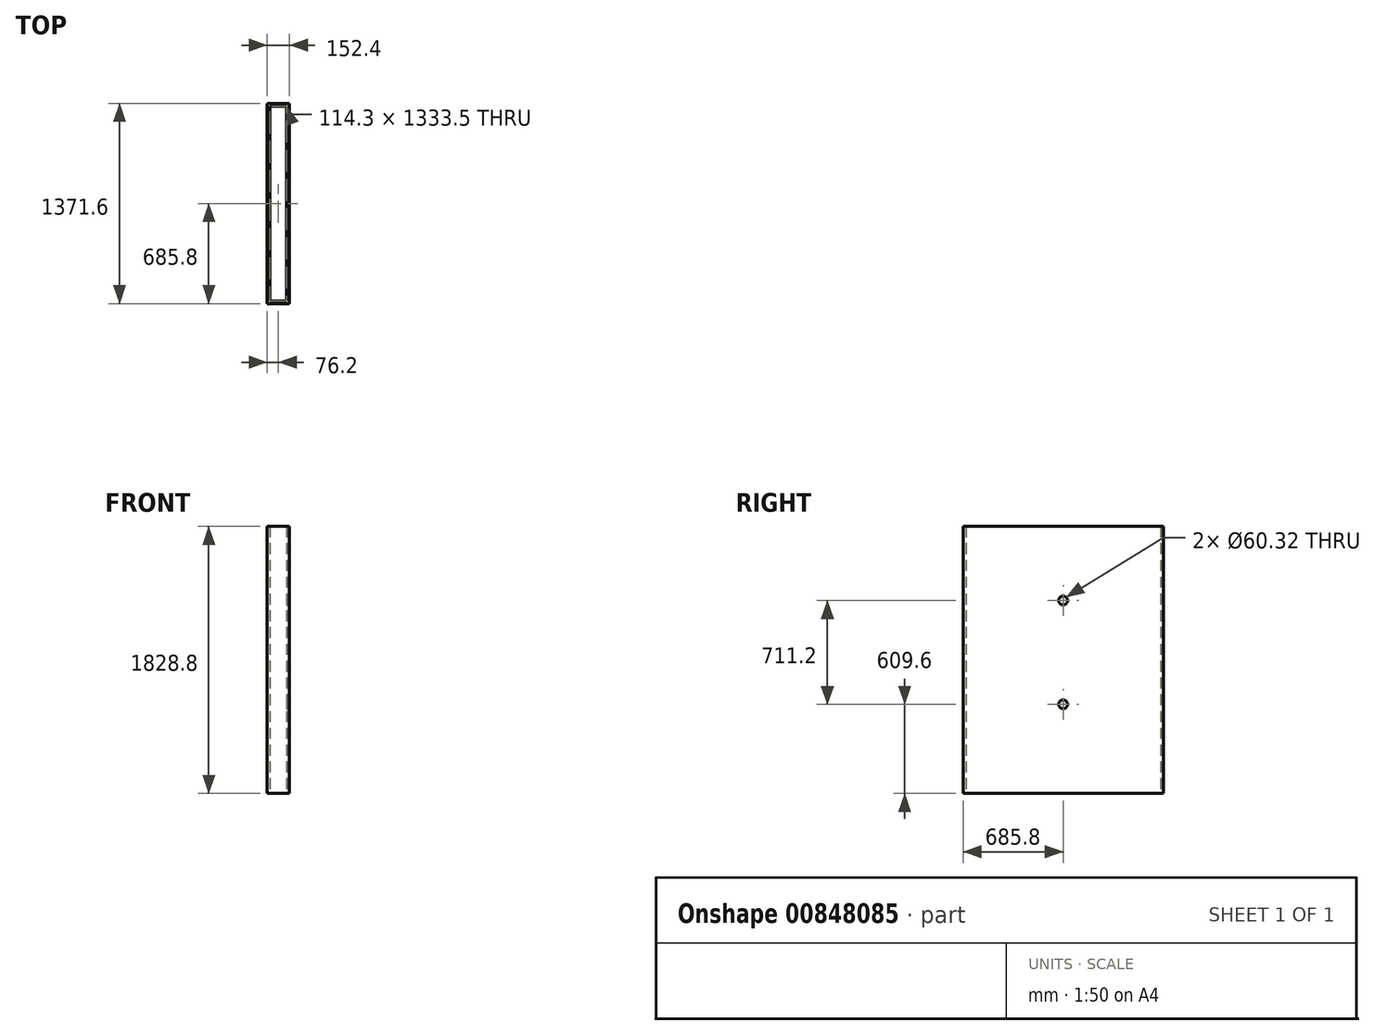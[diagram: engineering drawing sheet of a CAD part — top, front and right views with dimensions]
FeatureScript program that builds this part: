
annotation { "Feature Type Name" : "Feature", "Feature Type Description" : "" }
export const myFeature = defineFeature(function(context is Context, id is Id, definition is map)
    precondition{}
    {
        {
            var Q0;
            Q0=qCreatedBy(makeId("Top.planeOp"),FACE);
            var sketch = newSketch(context, id + "F0", { "sketchPlane" : qUnion([Q0])});
            skLineSegment(sketch, "E0.bottom", {"start": v(76.2, 685.8) * mm, "end": v(-76.2, 685.8) * mm});
            skLineSegment(sketch, "E0.top", {"start": v(76.2, -685.8) * mm, "end": v(-76.2, -685.8) * mm});
            skLineSegment(sketch, "E0.left", {"start": v(76.2, 685.8) * mm, "end": v(76.2, -685.8) * mm});
            skLineSegment(sketch, "E0.right", {"start": v(-76.2, 685.8) * mm, "end": v(-76.2, -685.8) * mm});
            skPoint(sketch, "E0.middle", {"position": v(0, 0) * mm});
            skLineSegment(sketch, "E1.bottom", {"start": v(57.15, -666.75) * mm, "end": v(-57.15, -666.75) * mm});
            skLineSegment(sketch, "E1.top", {"start": v(57.15, 666.75) * mm, "end": v(-57.15, 666.75) * mm});
            skLineSegment(sketch, "E1.left", {"start": v(57.15, -666.75) * mm, "end": v(57.15, 666.75) * mm});
            skLineSegment(sketch, "E1.right", {"start": v(-57.15, -666.75) * mm, "end": v(-57.15, 666.75) * mm});
            skSolve(sketch);
        }
        {
            var Q0;
            Q0=makeQuery(id+"F0.imprint","IMPRINT",FACE,{"disambiguationData":[TD([[makeQuery(id+"F0.imprint","IMPRINT",EDGE,{"derivedFrom":sQuery(id+"F0.wireOp",EDGE,"E0.bottom")}),1.0]])]});
            extrude(context, id + "F1", {"entities" : qUnion([Q0]), "depth" : 1828.8 * mm, "offsetDistance" : 25.4 * mm});
        }
        {
            var Q0;
            Q0=makeQuery(id+"F1.opExtrude","SWEPT_FACE",FACE,{"disambiguationData":[OSD([sQuery(id+"F0.wireOp",EDGE,"E0.left")])]});
            var sketch = newSketch(context, id + "F2", { "sketchPlane" : qUnion([Q0])});
            skLineSegment(sketch, "E2", {"start": v(0, 1828.8) * mm, "end": v(0, 1320.8) * mm});
            skLineSegment(sketch, "E3", {"start": v(0, 0) * mm, "end": v(0, 609.6) * mm});
            skCircle(sketch, "E4", {"center": v(0, 1320.8) * mm, "radius": 30.16 * mm});
            skCircle(sketch, "E5", {"center": v(0, 609.6) * mm, "radius": 30.16 * mm});
            skLineSegment(sketch, "E6", {"start": v(0, 0) * mm, "end": v(0, 101.6) * mm});
            skLineSegment(sketch, "E7", {"start": v(0, 101.6) * mm, "end": v(0, 419.1) * mm});
            skLineSegment(sketch, "E8.bottom", {"start": v(133.35, 419.1) * mm, "end": v(-133.35, 419.1) * mm});
            skLineSegment(sketch, "E8.top", {"start": v(133.35, 101.6) * mm, "end": v(-133.35, 101.6) * mm});
            skLineSegment(sketch, "E8.left", {"start": v(133.35, 419.1) * mm, "end": v(133.35, 101.6) * mm});
            skLineSegment(sketch, "E8.right", {"start": v(-133.35, 419.1) * mm, "end": v(-133.35, 101.6) * mm});
            skPoint(sketch, "E8.middle", {"position": v(0, 260.35) * mm});
            skSolve(sketch);
        }
        {
            var Q0;
            Q0=makeQuery(id+"F2.imprint","IMPRINT",FACE,{"disambiguationData":[TD([[makeQuery(id+"F2.imprint","IMPRINT",EDGE,{"derivedFrom":sQuery(id+"F2.wireOp",EDGE,"E4")}),1.0]])]});
            var Q1;
            Q1=makeQuery(id+"F2.imprint","IMPRINT",FACE,{"disambiguationData":[TD([[makeQuery(id+"F2.imprint","IMPRINT",EDGE,{"derivedFrom":sQuery(id+"F2.wireOp",EDGE,"E5")}),1.0]])]});
            var Q2;
            {var subQ0=sQuery(id+"F2.wireOp",EDGE,"E7");Q2=makeQuery(id+"F2.imprint","IMPRINT",FACE,{"disambiguationData":[TD([[makeQuery(id+"F2.imprint","IMPRINT",EDGE,{"derivedFrom":subQ0}),1.0]])]});}
            var Q3;
            {var subQ0=sQuery(id+"F2.wireOp",EDGE,"E7");Q3=makeQuery(id+"F2.imprint","IMPRINT",FACE,{"disambiguationData":[TD([[makeQuery(id+"F2.imprint","IMPRINT",EDGE,{"derivedFrom":subQ0}),-1.0]])]});}
            extrude(context, id + "F3", {"entities" : qUnion([Q0, Q1, Q2, Q3]), "operationType" : NewBodyOperationType.REMOVE, "oppositeDirection" : true, "depth" : 25.4 * mm, "offsetDistance" : 25.4 * mm});
        }
    });
